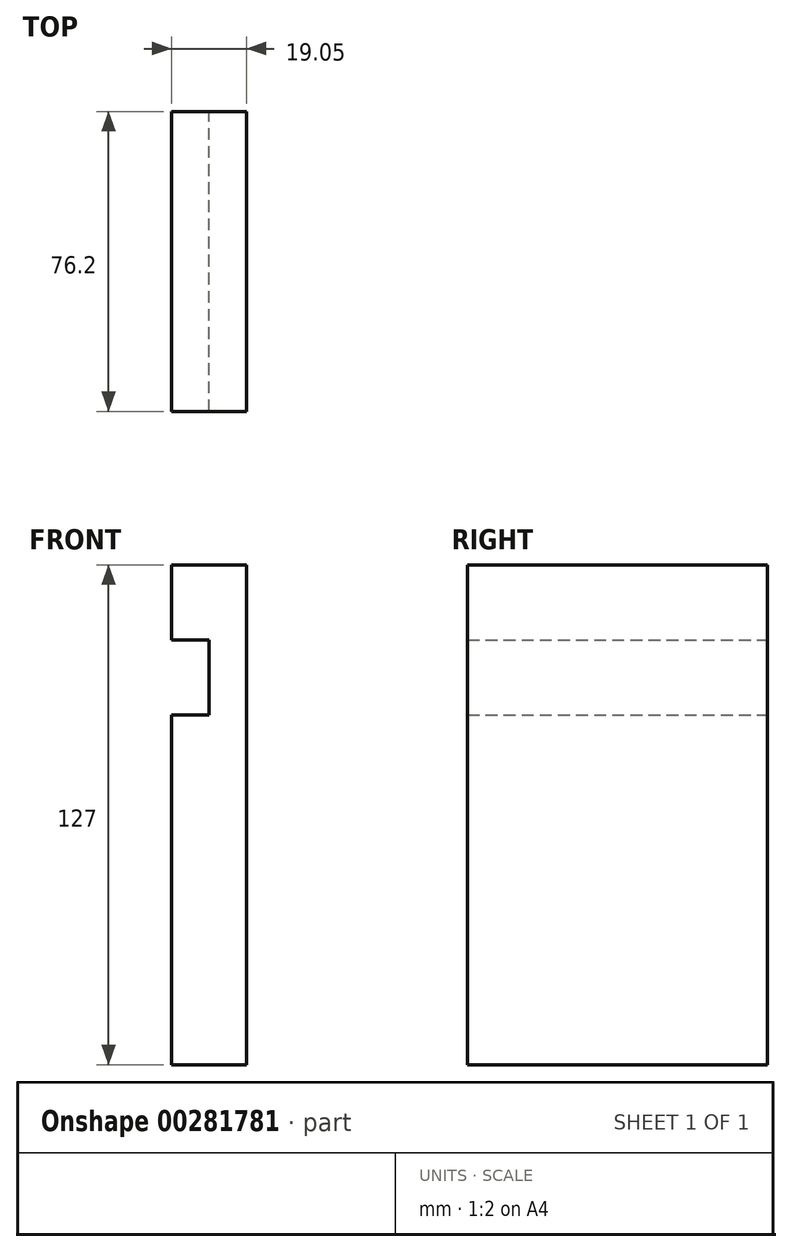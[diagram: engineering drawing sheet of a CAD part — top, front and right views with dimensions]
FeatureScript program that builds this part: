
annotation { "Feature Type Name" : "Feature", "Feature Type Description" : "" }
export const myFeature = defineFeature(function(context is Context, id is Id, definition is map)
    precondition{}
    {
        {
            var Q0;
            Q0=qCreatedBy(makeId("Front.planeOp"),FACE);
            var sketch = newSketch(context, id + "F0", { "sketchPlane" : qUnion([Q0])});
            skLineSegment(sketch, "E0", {"start": v(0, -83.38) * mm, "end": v(0, 5.52) * mm});
            skLineSegment(sketch, "E1", {"start": v(0, 43.62) * mm, "end": v(-19.05, 43.62) * mm});
            skLineSegment(sketch, "E2", {"start": v(-19.05, 43.62) * mm, "end": v(-19.05, 24.57) * mm});
            skLineSegment(sketch, "E3", {"start": v(0, -83.38) * mm, "end": v(-19.05, -83.38) * mm});
            skLineSegment(sketch, "E4", {"start": v(-19.05, -83.38) * mm, "end": v(-19.05, 5.52) * mm});
            skLineSegment(sketch, "E5.trimOffspring", {"start": v(0, 24.57) * mm, "end": v(0, 43.62) * mm});
            skLineSegment(sketch, "E6", {"start": v(-19.05, 24.57) * mm, "end": v(-9.52, 24.57) * mm});
            skLineSegment(sketch, "E7", {"start": v(-9.52, 24.57) * mm, "end": v(-9.52, 5.52) * mm});
            skLineSegment(sketch, "E8", {"start": v(-9.52, 5.52) * mm, "end": v(-19.05, 5.52) * mm});
            skLineSegment(sketch, "E9", {"start": v(0, 24.57) * mm, "end": v(0, 5.52) * mm});
            skSolve(sketch);
        }
        {
            var Q0;
            Q0 = qSketchRegion(id + "F0", true);
            extrude(context, id + "F1", {"entities" : qUnion([Q0]), "depth" : 76.2 * mm});
        }
    });
